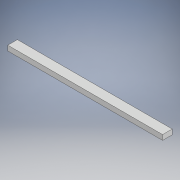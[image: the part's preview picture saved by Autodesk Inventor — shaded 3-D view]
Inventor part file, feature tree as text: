
AUTODESK INVENTOR PART (.ipt)
format: ipt  version: 2022.2 (Build 262287010, 287A)  size: 127,488 bytes
history: native  units: in
note: dims shown in document units (in); Inventor stores cm internally (conversion verified against a paired STEP export)
features: other x1, direct_edit x1, revolve x1
ambient origin geometry x8: Origin, YZ Plane, XZ Plane, XY Plane, X Axis, Y Axis, Z Axis, Center Point
bodies: Solid1 (feature_tree)
feature tree (3):
  other  "Head (L)"
  direct_edit  "Direct Edit1"
  revolve  "Rotate1"  Angle=90.0deg
